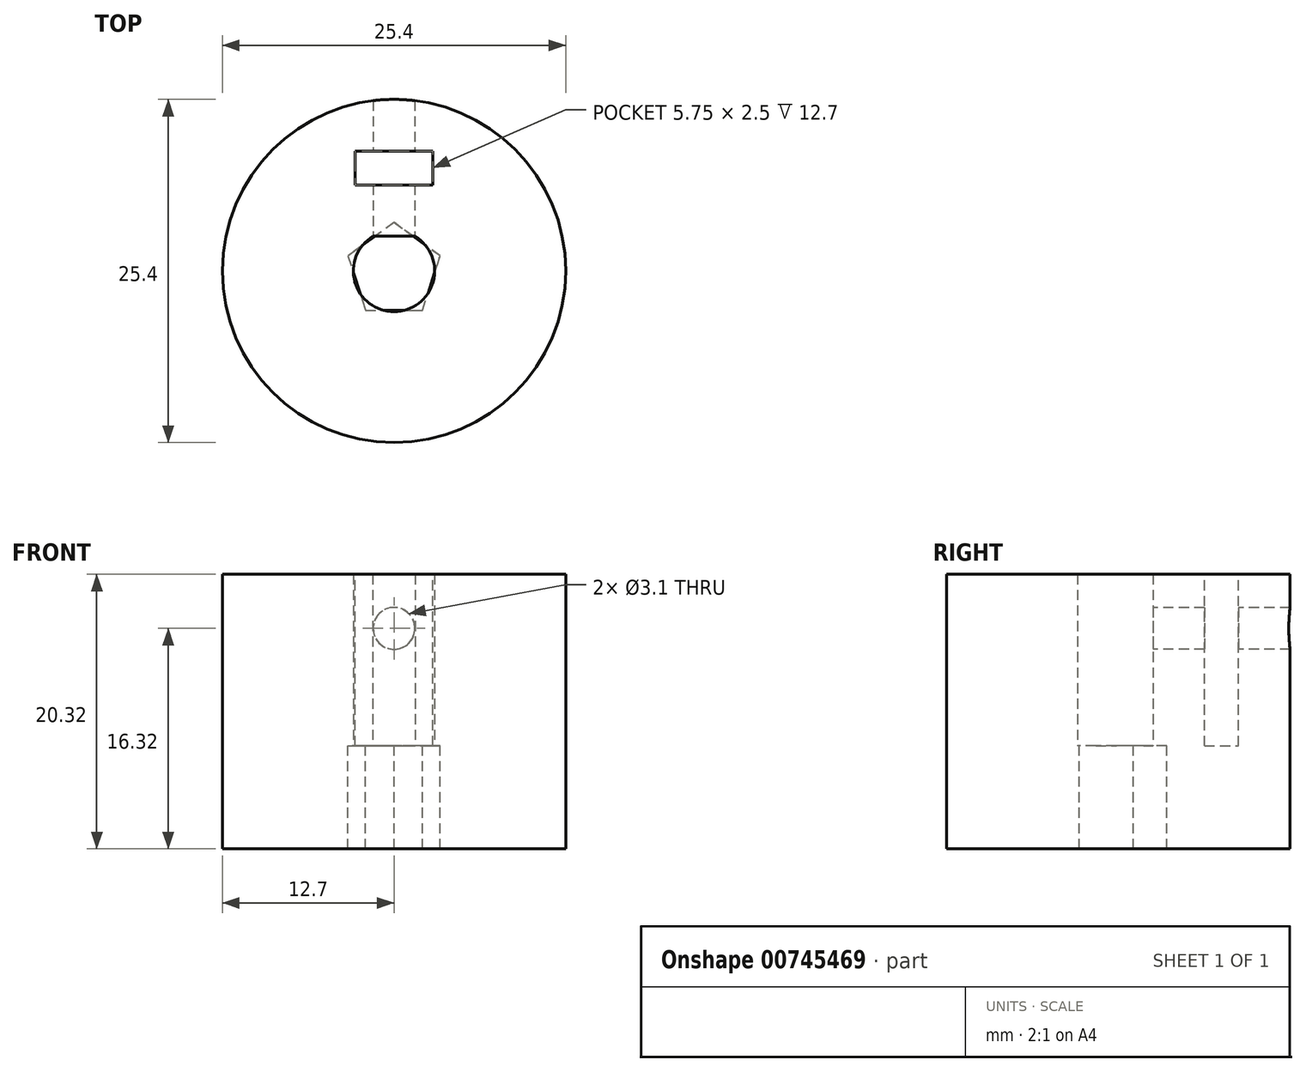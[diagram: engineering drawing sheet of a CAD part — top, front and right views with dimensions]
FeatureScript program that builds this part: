
annotation { "Feature Type Name" : "Feature", "Feature Type Description" : "" }
export const myFeature = defineFeature(function(context is Context, id is Id, definition is map)
    precondition{}
    {
        {
            var Q0;
            Q0=qCreatedBy(makeId("Top.planeOp"),FACE);
            var sketch = newSketch(context, id + "F0", { "sketchPlane" : qUnion([Q0])});
            skCircle(sketch, "E0", {"center": v(0, 0) * mm, "radius": 12.7 * mm});
            skArc(sketch, "E1", {"start": v(-1.57, 2.57) * mm, "mid": v(0, -3) * mm, "end": v(1.57, 2.57) * mm});
            skLineSegment(sketch, "E2", {"start": v(-1.57, 2.57) * mm, "end": v(1.57, 2.57) * mm});
            skSolve(sketch);
        }
        {
            var Q0;
            Q0 = qSketchRegion(id + "F0", true);
            extrude(context, id + "F1", {"entities" : qUnion([Q0]), "depth" : 12.7 * mm, "offsetDistance" : 25.4 * mm});
        }
        {
            var Q0;
            Q0=qCreatedBy(makeId("Front.planeOp"),FACE);
            var sketch = newSketch(context, id + "F2", { "sketchPlane" : qUnion([Q0])});
            skLineSegment(sketch, "E3", {"start": v(0, 0) * mm, "end": v(0, 12.7) * mm, "construction": true});
            skCircle(sketch, "E4", {"center": v(0, 8.7) * mm, "radius": 1.55 * mm});
            skSolve(sketch);
        }
        {
            var Q0;
            Q0 = qSketchRegion(id + "F2", true);
            extrude(context, id + "F3", {"entities" : qUnion([Q0]), "operationType" : NewBodyOperationType.REMOVE, "endBound" : BoundingType.THROUGH_ALL, "oppositeDirection" : true, "depth" : 25.4 * mm, "offsetDistance" : 25.4 * mm});
        }
        {
            var Q0;
            Q0=makeQuery(id+"F1.opExtrude","CAP_FACE",FACE,{"disambiguationData":[OSD([sQuery(id+"F0.wireOp",EDGE,"E0"),sQuery(id+"F0.wireOp",EDGE,"E1"),sQuery(id+"F0.wireOp",EDGE,"E2")])],"isStart":false});
            var sketch = newSketch(context, id + "F4", { "sketchPlane" : qUnion([Q0])});
            skLineSegment(sketch, "E5.bottom", {"start": v(2.87, 6.37) * mm, "end": v(-2.88, 6.37) * mm});
            skLineSegment(sketch, "E5.top", {"start": v(2.87, 8.87) * mm, "end": v(-2.88, 8.87) * mm});
            skLineSegment(sketch, "E5.left", {"start": v(2.87, 6.37) * mm, "end": v(2.87, 8.87) * mm});
            skLineSegment(sketch, "E5.right", {"start": v(-2.88, 6.37) * mm, "end": v(-2.88, 8.87) * mm});
            skPoint(sketch, "E5.middle", {"position": v(0, 7.62) * mm});
            skSolve(sketch);
        }
        {
            var Q0;
            Q0 = qSketchRegion(id + "F4", true);
            extrude(context, id + "F5", {"entities" : qUnion([Q0]), "operationType" : NewBodyOperationType.REMOVE, "endBound" : BoundingType.THROUGH_ALL, "oppositeDirection" : true, "depth" : 10.16 * mm, "offsetDistance" : 25.4 * mm});
        }
        {
            var Q0;
            Q0=makeQuery(id+"F1.opExtrude","CAP_FACE",FACE,{"disambiguationData":[OSD([sQuery(id+"F0.wireOp",EDGE,"E0"),sQuery(id+"F0.wireOp",EDGE,"E1"),sQuery(id+"F0.wireOp",EDGE,"E2")])],"isStart":true});
            var sketch = newSketch(context, id + "F6", { "sketchPlane" : qUnion([Q0])});
            skCircle(sketch, "E6", {"center": v(0, 0) * mm, "radius": 12.7 * mm});
            skCircle(sketch, "E7.cCircle", {"center": v(0, 0) * mm, "radius": 2.9 * mm, "construction": true});
            skLineSegment(sketch, "E7.0", {"start": v(-3.4, -1.1) * mm, "end": v(-2.1, 2.9) * mm});
            skLineSegment(sketch, "E7.1", {"start": v(-2.1, 2.9) * mm, "end": v(2.1, 2.9) * mm});
            skLineSegment(sketch, "E7.2", {"start": v(2.1, 2.9) * mm, "end": v(3.4, -1.1) * mm});
            skLineSegment(sketch, "E7.3", {"start": v(3.4, -1.1) * mm, "end": v(0, -3.58) * mm});
            skLineSegment(sketch, "E7.4", {"start": v(0, -3.58) * mm, "end": v(-3.4, -1.1) * mm});
            skPoint(sketch, "E7.0.midPoint", {"position": v(-2.76, 0.9) * mm});
            skSolve(sketch);
        }
        {
            var Q0;
            Q0 = qSketchRegion(id + "F6", true);
            extrude(context, id + "F7", {"entities" : qUnion([Q0]), "operationType" : NewBodyOperationType.ADD, "depth" : 7.62 * mm, "offsetDistance" : 25.4 * mm});
        }
        {
            var Q0;
            Q0=makeQuery(id+"F1.opExtrude","CAP_FACE",FACE,{"disambiguationData":[OSD([sQuery(id+"F0.wireOp",EDGE,"E0"),sQuery(id+"F0.wireOp",EDGE,"E1"),sQuery(id+"F0.wireOp",EDGE,"E2")])],"isStart":false});
            var Q1;
            Q1=makeQuery(id+"F7.opExtrude","CAP_FACE",FACE,{"disambiguationData":[OSD([sQuery(id+"F6.wireOp",EDGE,"E6"),sQuery(id+"F6.wireOp",EDGE,"e4bb7ca1-57e4-48af-88d4-4abb3308b77c.0"),sQuery(id+"F6.wireOp",EDGE,"e4bb7ca1-57e4-48af-88d4-4abb3308b77c.1"),sQuery(id+"F6.wireOp",EDGE,"e4bb7ca1-57e4-48af-88d4-4abb3308b77c.2"),sQuery(id+"F6.wireOp",EDGE,"e4bb7ca1-57e4-48af-88d4-4abb3308b77c.3"),sQuery(id+"F6.wireOp",EDGE,"e4bb7ca1-57e4-48af-88d4-4abb3308b77c.4")])],"isStart":false});
            cPlane(context, id + "F8", {"entities" : qUnion([Q0, Q1]), "cplaneType" : CPlaneType.MID_PLANE, "offset" : 25.4 * mm, "width" : 152.4 * mm, "height" : 152.4 * mm});
        }
    });
